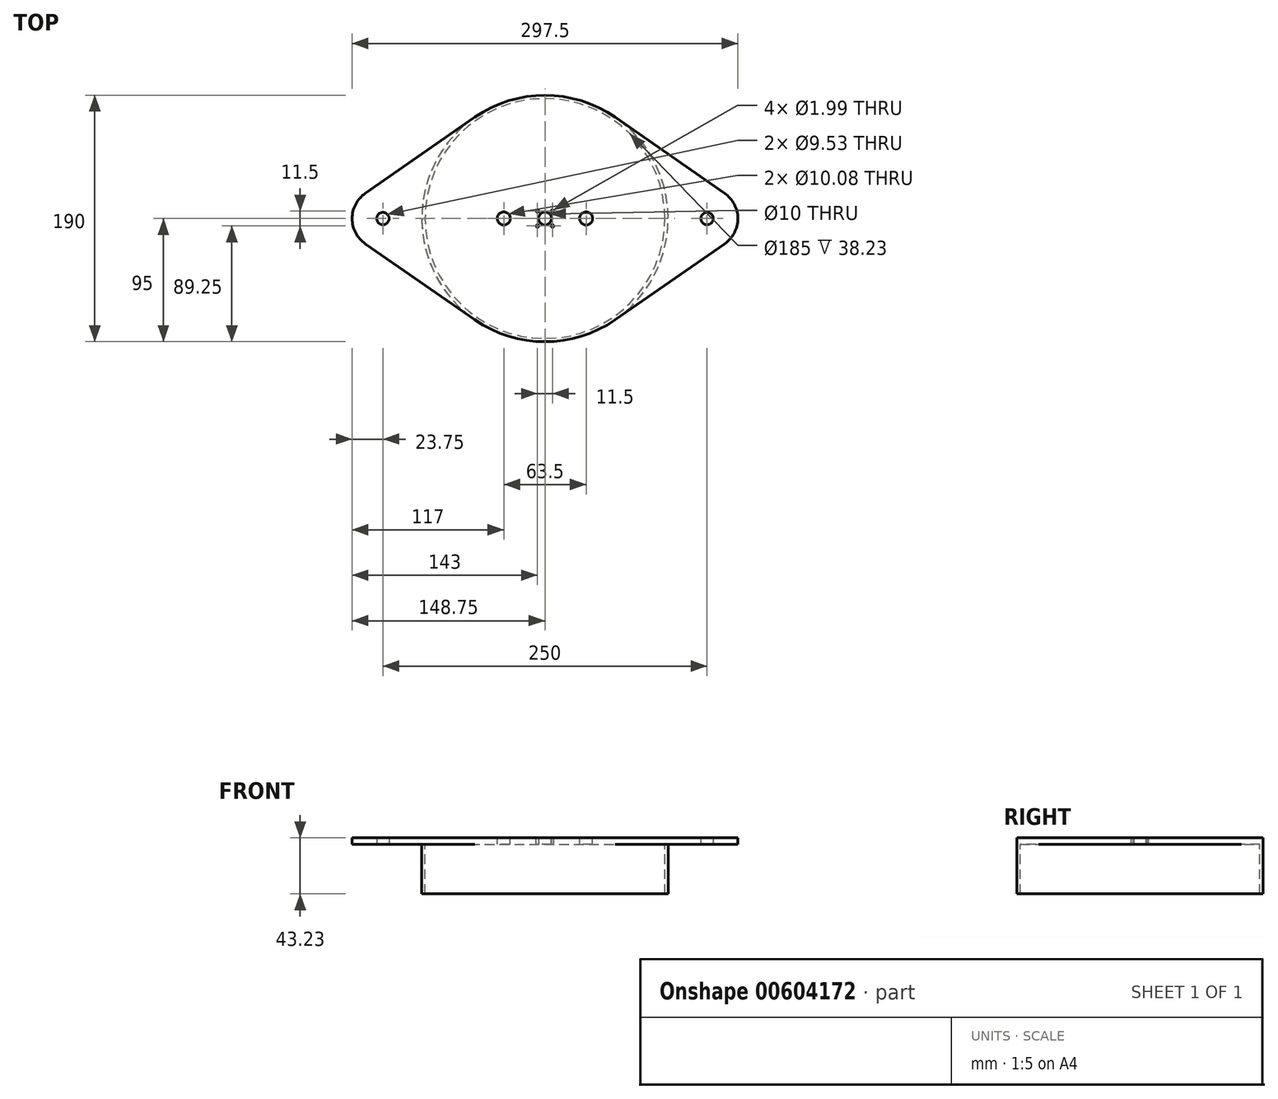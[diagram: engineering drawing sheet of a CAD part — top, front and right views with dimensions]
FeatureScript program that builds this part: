
annotation { "Feature Type Name" : "Feature", "Feature Type Description" : "" }
export const myFeature = defineFeature(function(context is Context, id is Id, definition is map)
    precondition{}
    {
        {
            var Q0;
            Q0=qCreatedBy(makeId("Top.planeOp"),FACE);
            var sketch = newSketch(context, id + "F0", { "sketchPlane" : qUnion([Q0])});
            skCircle(sketch, "E0", {"center": v(0, 0) * mm, "radius": 95 * mm});
            skLineSegment(sketch, "E1", {"start": v(-125, 0) * mm, "end": v(125, 0) * mm, "construction": true});
            skCircle(sketch, "E2", {"center": v(-125, 0) * mm, "radius": 23.75 * mm});
            skCircle(sketch, "E3", {"center": v(125, 0) * mm, "radius": 23.75 * mm});
            skCircle(sketch, "E4", {"center": v(0, 0) * mm, "radius": 5 * mm});
            skLineSegment(sketch, "E5", {"start": v(-138.54, 19.51) * mm, "end": v(-54.15, 78.06) * mm});
            skLineSegment(sketch, "E6", {"start": v(138.54, 19.51) * mm, "end": v(54.15, 78.06) * mm});
            skLineSegment(sketch, "E7", {"start": v(-138.54, -19.51) * mm, "end": v(-54.15, -78.06) * mm});
            skLineSegment(sketch, "E8", {"start": v(138.54, -19.51) * mm, "end": v(54.15, -78.06) * mm});
            skCircle(sketch, "E9", {"center": v(-125, 0) * mm, "radius": 4.76 * mm});
            skCircle(sketch, "E10", {"center": v(125, 0) * mm, "radius": 4.76 * mm});
            skSolve(sketch);
        }
        {
            var Q0;
            Q0 = qSketchRegion(id + "F0", true);
            extrude(context, id + "F1", {"entities" : qUnion([Q0]), "depth" : 5 * mm, "offsetDistance" : 25 * mm});
        }
        {
            var Q0;
            Q0=makeQuery(id+"F1.opExtrude","CAP_FACE",FACE,{"disambiguationData":[OSD([sQuery(id+"F0.wireOp",EDGE,"E0"),sQuery(id+"F0.wireOp",EDGE,"E2"),sQuery(id+"F0.wireOp",EDGE,"E3"),sQuery(id+"F0.wireOp",EDGE,"E4"),sQuery(id+"F0.wireOp",EDGE,"E5"),sQuery(id+"F0.wireOp",EDGE,"E6"),sQuery(id+"F0.wireOp",EDGE,"E7"),sQuery(id+"F0.wireOp",EDGE,"E8")])],"isStart":true});
            var sketch = newSketch(context, id + "F2", { "sketchPlane" : qUnion([Q0])});
            skCircle(sketch, "E11", {"center": v(0, 0) * mm, "radius": 95 * mm});
            skCircle(sketch, "E12", {"center": v(0, 0) * mm, "radius": 92.5 * mm});
            skSolve(sketch);
        }
        {
            var Q0;
            Q0 = qSketchRegion(id + "F2", true);
            extrude(context, id + "F3", {"entities" : qUnion([Q0]), "operationType" : NewBodyOperationType.ADD, "depth" : 38.23 * mm, "offsetDistance" : 25 * mm});
        }
        {
            var Q0;
            Q0=makeQuery(id+"F1.opExtrude","CAP_FACE",FACE,{"disambiguationData":[OSD([sQuery(id+"F0.wireOp",EDGE,"E0"),sQuery(id+"F0.wireOp",EDGE,"E2"),sQuery(id+"F0.wireOp",EDGE,"E3"),sQuery(id+"F0.wireOp",EDGE,"E4"),sQuery(id+"F0.wireOp",EDGE,"E5"),sQuery(id+"F0.wireOp",EDGE,"E6"),sQuery(id+"F0.wireOp",EDGE,"E7"),sQuery(id+"F0.wireOp",EDGE,"E8")])],"isStart":false});
            var sketch = newSketch(context, id + "F4", { "sketchPlane" : qUnion([Q0])});
            skLineSegment(sketch, "E13.bottom", {"start": v(5.75, 5.75) * mm, "end": v(-5.75, 5.75) * mm, "construction": true});
            skLineSegment(sketch, "E13.top", {"start": v(5.75, -5.75) * mm, "end": v(-5.75, -5.75) * mm, "construction": true});
            skLineSegment(sketch, "E13.left", {"start": v(5.75, 5.75) * mm, "end": v(5.75, -5.75) * mm, "construction": true});
            skLineSegment(sketch, "E13.right", {"start": v(-5.75, 5.75) * mm, "end": v(-5.75, -5.75) * mm, "construction": true});
            skPoint(sketch, "E13.middle", {"position": v(0, 0) * mm});
            skSolve(sketch);
        }
        {
            var Q0;
            Q0=makeQuery(id+"F4.imprint","IMPRINT",FACE,{"disambiguationData":[TD([[makeQuery(id+"F4.imprint","IMPRINT",EDGE,{"derivedFrom":makeQuery(id+"F1.opExtrude","CAP_EDGE",EDGE,{"disambiguationData":[OSD([sQuery(id+"F0.wireOp",EDGE,"E2")])],"isStart":false})}),1.0]])]});
            var sketch = newSketch(context, id + "F5", { "sketchPlane" : qUnion([Q0])});
            skLineSegment(sketch, "E14", {"start": v(-31.75, 0) * mm, "end": v(31.75, 0) * mm, "construction": true});
            skSolve(sketch);
        }
        {
            var Q0;
            Q0=sQuery(id+"F4.wireOp",VERTEX,"E13.right.start");
            var Q1;
            Q1=sQuery(id+"F4.wireOp",VERTEX,"E13.left.start");
            var Q2;
            Q2=sQuery(id+"F4.wireOp",VERTEX,"E13.top.start");
            var Q3;
            Q3=sQuery(id+"F4.wireOp",VERTEX,"E13.top.end");
            var Q4;
            Q4=makeQuery(id+"F1.opExtrude","SWEPT_BODY",BODY,{"disambiguationData":[OSD([sQuery(id+"F0.wireOp",EDGE,"E0"),sQuery(id+"F0.wireOp",EDGE,"E2"),sQuery(id+"F0.wireOp",EDGE,"E3"),sQuery(id+"F0.wireOp",EDGE,"E4"),sQuery(id+"F0.wireOp",EDGE,"E5"),sQuery(id+"F0.wireOp",EDGE,"E6"),sQuery(id+"F0.wireOp",EDGE,"E7"),sQuery(id+"F0.wireOp",EDGE,"E8")])]});
            hole(context, id + "F6", {"style" : HoleStyle.SIMPLE, "endStyle" : HoleEndStyle.BLIND, "standardTappedOrClearance" : lookupTablePath({ "standard" : "ANSI", "engagement" : "75%", "pitch" : "48 tpi", "size" : "#3", "type" : "Tapped" }), "standardBlindInLast" : lookupTablePath({ "standard" : "ANSI", "engagement" : "75%", "pitch" : "48 tpi", "size" : "#3", "type" : "Tapped" }), "holeDiameter" : 2 * mm, "majorDiameter" : 2.5 * mm, "showTappedDepth" : true, "holeDepth" : 13.6 * mm, "isTappedThrough" : true, "tappedDepth" : 12 * mm, "tapClearance" : 3, "locations" : qUnion([Q0, Q1, Q2, Q3]), "scope" : qUnion([Q4])});
        }
        {
            var Q0;
            Q0=sQuery(id+"F5.wireOp",VERTEX,"E14.start");
            var Q1;
            Q1=sQuery(id+"F5.wireOp",VERTEX,"E14.end");
            var Q2;
            Q2=makeQuery(id+"F1.opExtrude","SWEPT_BODY",BODY,{"disambiguationData":[OSD([sQuery(id+"F0.wireOp",EDGE,"E0"),sQuery(id+"F0.wireOp",EDGE,"E2"),sQuery(id+"F0.wireOp",EDGE,"E3"),sQuery(id+"F0.wireOp",EDGE,"E4"),sQuery(id+"F0.wireOp",EDGE,"E5"),sQuery(id+"F0.wireOp",EDGE,"E6"),sQuery(id+"F0.wireOp",EDGE,"E7"),sQuery(id+"F0.wireOp",EDGE,"E8")])]});
            hole(context, id + "F7", {"style" : HoleStyle.SIMPLE, "endStyle" : HoleEndStyle.BLIND, "standardTappedOrClearance" : lookupTablePath({ "standard" : "ANSI", "fit" : "Normal (ASME)", "size" : "3/8", "type" : "Clearance" }), "standardBlindInLast" : lookupTablePath({ "fit" : "Free", "standard" : "ANSI", "size" : "3/8", "type" : "Clearance" }), "holeDiameter" : 10.08 * mm, "majorDiameter" : 2.5 * mm, "holeDepth" : 13.6 * mm, "isTappedThrough" : true, "tappedDepth" : 12 * mm, "tapClearance" : 3, "locations" : qUnion([Q0, Q1]), "scope" : qUnion([Q2])});
        }
    });
